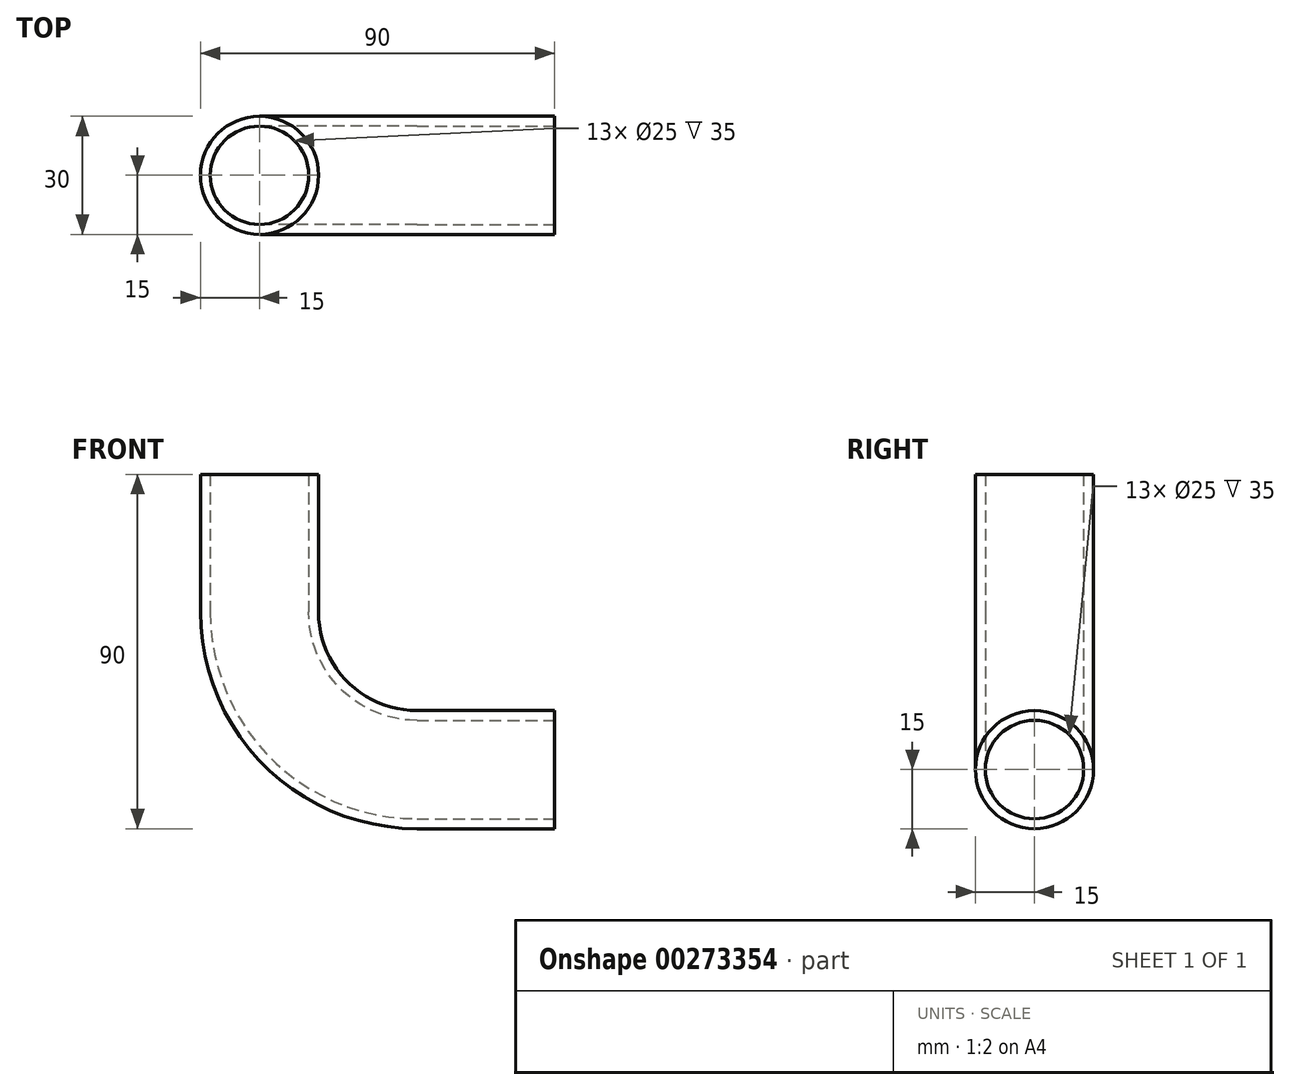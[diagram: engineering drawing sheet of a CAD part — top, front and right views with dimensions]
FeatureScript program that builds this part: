
annotation { "Feature Type Name" : "Feature", "Feature Type Description" : "" }
export const myFeature = defineFeature(function(context is Context, id is Id, definition is map)
    precondition{}
    {
        {
            var Q0;
            Q0=qCreatedBy(makeId("Front.planeOp"),FACE);
            var sketch = newSketch(context, id + "F0", { "sketchPlane" : qUnion([Q0])});
            skLineSegment(sketch, "E0", {"start": v(0, 75) * mm, "end": v(0, 40) * mm});
            skLineSegment(sketch, "E1", {"start": v(40, 0) * mm, "end": v(75, 0) * mm});
            skPoint(sketch, "E2.visualSharp", {"position": v(0, 0) * mm});
            skArc(sketch, "E2.filletArc", {"start": v(0, 40) * mm, "mid": v(11.72, 11.72) * mm, "end": v(40, 0) * mm});
            skSolve(sketch);
        }
        {
            var Q0;
            Q0=sQuery(id+"F0.wireOp",EDGE,"E0");
            var Q1;
            Q1=sQuery(id+"F0.wireOp",VERTEX,"E0.start");
            cPlane(context, id + "F1", {"entities" : qUnion([Q0, Q1]), "cplaneType" : CPlaneType.LINE_POINT, "offset" : 25 * mm, "width" : 150 * mm, "height" : 150 * mm});
        }
        {
            var Q0;
            Q0=qCreatedBy(id+"F1.planeOp",FACE);
            var sketch = newSketch(context, id + "F2", { "sketchPlane" : qUnion([Q0])});
            skCircle(sketch, "E3", {"center": v(0, 0) * mm, "radius": 15 * mm});
            skSolve(sketch);
        }
        {
            var Q0;
            Q0=makeQuery(id+"F2.imprint","IMPRINT",FACE,{"disambiguationData":[TD([[makeQuery(id+"F2.imprint","IMPRINT",EDGE,{"derivedFrom":sQuery(id+"F2.wireOp",EDGE,"E3")}),1.0]])]});
            var Q1;
            Q1=sQuery(id+"F0.wireOp",EDGE,"E0");
            var Q2;
            Q2=sQuery(id+"F0.wireOp",EDGE,"E2.filletArc");
            var Q3;
            Q3=sQuery(id+"F0.wireOp",EDGE,"E1");
            sweep(context, id + "F3", {"profiles" : qUnion([Q0]), "path" : qUnion([Q1, Q2, Q3])});
        }
        {
            var Q0;
            Q0=makeQuery(id+"F3.opSweep","CAP_FACE",FACE,{"disambiguationData":[OSD([sQuery(id+"F0.wireOp",VERTEX,"E1.end"),sQuery(id+"F2.wireOp",EDGE,"E3")])],"isStart":false});
            var Q1;
            Q1=makeQuery(id+"F3.opSweep","CAP_FACE",FACE,{"disambiguationData":[OSD([sQuery(id+"F0.wireOp",VERTEX,"E0.start"),sQuery(id+"F2.wireOp",EDGE,"E3")])],"isStart":true});
            shell(context, id + "F4", {"entities" : qUnion([Q0, Q1]), "thickness" : 2.5 * mm});
        }
    });
